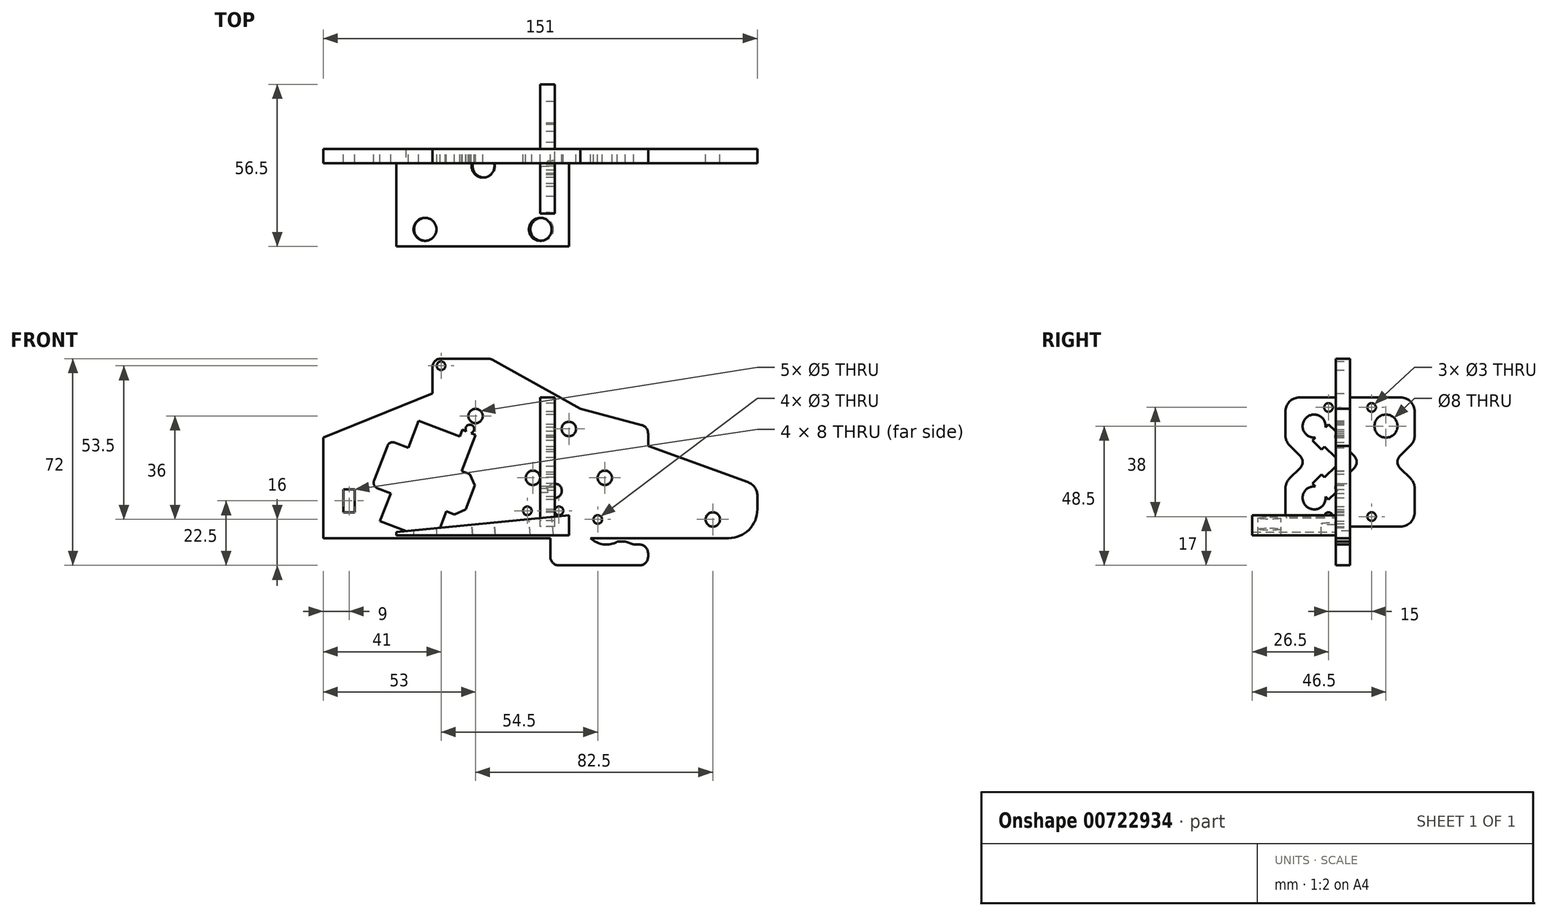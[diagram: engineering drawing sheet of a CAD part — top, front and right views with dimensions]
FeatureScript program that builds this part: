
annotation { "Feature Type Name" : "Feature", "Feature Type Description" : "" }
export const myFeature = defineFeature(function(context is Context, id is Id, definition is map)
    precondition{}
    {
        {
            var Q0;
            Q0=qCreatedBy(makeId("Front.planeOp"),FACE);
            var sketch = newSketch(context, id + "F0", { "sketchPlane" : qUnion([Q0])});
            skLineSegment(sketch, "E0", {"start": v(-50.05, -25.56) * mm, "end": v(9.95, -25.56) * mm});
            skLineSegment(sketch, "E1", {"start": v(9.95, -25.56) * mm, "end": v(9.95, -18.56) * mm});
            skLineSegment(sketch, "E2", {"start": v(-50.05, -25.56) * mm, "end": v(-50.05, -24.36) * mm});
            skLineSegment(sketch, "E3", {"start": v(9.95, -18.56) * mm, "end": v(-50.05, -24.36) * mm});
            skSolve(sketch);
        }
        {
            var Q0;
            Q0=makeQuery(id+"F0.imprint","IMPRINT",FACE,{"disambiguationData":[TD([[makeQuery(id+"F0.imprint","IMPRINT",EDGE,{"derivedFrom":sQuery(id+"F0.wireOp",EDGE,"E0")}),1.0]])]});
            extrude(context, id + "F1", {"entities" : qUnion([Q0]), "depth" : 34 * mm, "offsetDistance" : 25 * mm});
        }
        {
            var Q0;
            Q0=makeQuery(id+"F1.opExtrude","SWEPT_FACE",FACE,{"disambiguationData":[OSD([sQuery(id+"F0.wireOp",EDGE,"E3")])]});
            var sketch = newSketch(context, id + "F2", { "sketchPlane" : qUnion([Q0])});
            skCircle(sketch, "E4", {"center": v(-21.89, -6) * mm, "radius": 4 * mm});
            skCircle(sketch, "E5", {"center": v(-42.17, -28) * mm, "radius": 4 * mm});
            skCircle(sketch, "E6", {"center": v(-1.89, -28) * mm, "radius": 4 * mm});
            skSolve(sketch);
        }
        {
            var Q0;
            Q0 = qSketchRegion(id + "F2", true);
            extrude(context, id + "F3", {"entities" : qUnion([Q0]), "operationType" : NewBodyOperationType.REMOVE, "endBound" : BoundingType.THROUGH_ALL, "oppositeDirection" : true, "depth" : 25 * mm, "offsetDistance" : 25 * mm});
        }
        {
            var Q0;
            Q0=qCreatedBy(makeId("Front.planeOp"),FACE);
            var sketch = newSketch(context, id + "F4", { "sketchPlane" : qUnion([Q0])});
            skCircle(sketch, "E7", {"center": v(-68.5, -1) * mm, "radius": 2.5 * mm});
            skCircle(sketch, "E8", {"center": v(-22.5, 16) * mm, "radius": 2.5 * mm});
            skCircle(sketch, "E9", {"center": v(5, -10) * mm, "radius": 2.5 * mm});
            skCircle(sketch, "E10", {"center": v(20, -20) * mm, "radius": 1.5 * mm});
            skCircle(sketch, "E11", {"center": v(60, -20) * mm, "radius": 2.5 * mm});
            skArc(sketch, "E12", {"start": v(-50.58, 6.78) * mm, "mid": v(-52.11, 6.74) * mm, "end": v(-53.17, 5.63) * mm});
            skArc(sketch, "E13", {"start": v(-57.82, -6.5) * mm, "mid": v(-57.78, -8.04) * mm, "end": v(-56.67, -9.1) * mm});
            skArc(sketch, "E14", {"start": v(75.5, -11.74) * mm, "mid": v(74.6, -8.87) * mm, "end": v(72.21, -7.04) * mm});
            skArc(sketch, "E15", {"start": v(65.5, -26.5) * mm, "mid": v(72.57, -23.57) * mm, "end": v(75.5, -16.5) * mm});
            skArc(sketch, "E16", {"start": v(-18.3, 25.9) * mm, "mid": v(-19.98, 26.35) * mm, "end": v(-21.71, 26.5) * mm});
            skArc(sketch, "E17", {"start": v(-29, 26.5) * mm, "mid": v(-30.91, 26.32) * mm, "end": v(-32.75, 25.77) * mm});
            skLineSegment(sketch, "E18", {"start": v(-75.5, 8.5) * mm, "end": v(-32.75, 25.77) * mm});
            skLineSegment(sketch, "E19", {"start": v(-29, 26.5) * mm, "end": v(-21.71, 26.5) * mm});
            skLineSegment(sketch, "E20", {"start": v(-75.5, 8.5) * mm, "end": v(-75.5, -26.5) * mm});
            skLineSegment(sketch, "E21", {"start": v(-75.5, -26.5) * mm, "end": v(65.5, -26.5) * mm});
            skLineSegment(sketch, "E22", {"start": v(75.5, -11.74) * mm, "end": v(75.5, -16.5) * mm});
            skLineSegment(sketch, "E23", {"start": v(-18.3, 25.9) * mm, "end": v(72.21, -7.04) * mm});
            skLineSegment(sketch, "E24", {"start": v(-55.74, -20.62) * mm, "end": v(-46.4, -24.2) * mm});
            skLineSegment(sketch, "E25", {"start": v(-53.17, 5.63) * mm, "end": v(-57.82, -6.5) * mm});
            skLineSegment(sketch, "E26", {"start": v(-68.5, -9.5) * mm, "end": v(-64.5, -9.5) * mm});
            skLineSegment(sketch, "E27", {"start": v(-68.5, -9.5) * mm, "end": v(-68.5, -17.5) * mm});
            skLineSegment(sketch, "E28", {"start": v(-68.5, -17.5) * mm, "end": v(-64.5, -17.5) * mm});
            skLineSegment(sketch, "E29", {"start": v(-64.5, -9.5) * mm, "end": v(-64.5, -17.5) * mm});
            skLineSegment(sketch, "E30", {"start": v(-56.67, -9.1) * mm, "end": v(-52, -10.88) * mm});
            skLineSegment(sketch, "E31", {"start": v(-50.58, 6.78) * mm, "end": v(-45.91, 4.99) * mm});
            skLineSegment(sketch, "E32", {"start": v(-42.3, 14.4) * mm, "end": v(-28.02, 8.9) * mm});
            skLineSegment(sketch, "E33", {"start": v(-26, -16.51) * mm, "end": v(-22.77, -8.11) * mm});
            skLineSegment(sketch, "E34", {"start": v(-29.87, -18.24) * mm, "end": v(-32.67, -17.16) * mm});
            skLineSegment(sketch, "E35", {"start": v(-27.3, -3.16) * mm, "end": v(-24.5, -4.24) * mm});
            skLineSegment(sketch, "E36", {"start": v(-27.3, -3.16) * mm, "end": v(-23.35, 7.12) * mm});
            skLineSegment(sketch, "E37", {"start": v(-45.91, 4.99) * mm, "end": v(-42.3, 14.4) * mm});
            skLineSegment(sketch, "E38", {"start": v(-24.5, -4.24) * mm, "end": v(-22.77, -8.11) * mm});
            skLineSegment(sketch, "E39", {"start": v(-26, -16.51) * mm, "end": v(-29.87, -18.24) * mm});
            skLineSegment(sketch, "E40", {"start": v(-52, -10.88) * mm, "end": v(-55.74, -20.62) * mm});
            skLineSegment(sketch, "E41", {"start": v(-28.02, 8.9) * mm, "end": v(-27.12, 11.24) * mm});
            skLineSegment(sketch, "E42", {"start": v(-27.12, 11.24) * mm, "end": v(-22.46, 9.45) * mm});
            skLineSegment(sketch, "E43", {"start": v(-23.35, 7.12) * mm, "end": v(-22.46, 9.45) * mm});
            skLineSegment(sketch, "E44", {"start": v(-35.9, -25.56) * mm, "end": v(-40.56, -23.77) * mm});
            skLineSegment(sketch, "E45", {"start": v(-46.4, -24.2) * mm, "end": v(-40.56, -23.77) * mm});
            skLineSegment(sketch, "E46", {"start": v(-35.9, -25.56) * mm, "end": v(-32.67, -17.16) * mm});
            skSolve(sketch);
        }
        {
            var Q0;
            Q0=makeQuery(id+"F4.imprint","IMPRINT",FACE,{"disambiguationData":[TD([[makeQuery(id+"F4.imprint","IMPRINT",EDGE,{"derivedFrom":sQuery(id+"F4.wireOp",EDGE,"E7")}),1.0]])]});
            extrude(context, id + "F5", {"entities" : qUnion([Q0]), "operationType" : NewBodyOperationType.ADD, "depth" : 5 * mm, "offsetDistance" : 25 * mm});
        }
        {
            var Q0;
            Q0=qCreatedBy(makeId("Front.planeOp"),FACE);
            var sketch = newSketch(context, id + "F6", { "sketchPlane" : qUnion([Q0])});
            skCircle(sketch, "E47", {"center": v(-68.5, -1) * mm, "radius": 2.5 * mm});
            skCircle(sketch, "E48", {"center": v(-22.5, 16) * mm, "radius": 2.5 * mm});
            skCircle(sketch, "E49", {"center": v(5, -10) * mm, "radius": 2.5 * mm});
            skCircle(sketch, "E50", {"center": v(20, -20) * mm, "radius": 1.5 * mm});
            skCircle(sketch, "E51", {"center": v(60, -20) * mm, "radius": 2.5 * mm});
            skArc(sketch, "E52", {"start": v(-50.58, 6.78) * mm, "mid": v(-52.11, 6.74) * mm, "end": v(-53.17, 5.63) * mm});
            skArc(sketch, "E53", {"start": v(-57.82, -6.5) * mm, "mid": v(-57.78, -8.04) * mm, "end": v(-56.67, -9.1) * mm});
            skArc(sketch, "E54", {"start": v(75.5, -11.74) * mm, "mid": v(74.6, -8.87) * mm, "end": v(72.21, -7.04) * mm});
            skArc(sketch, "E55", {"start": v(65.5, -26.5) * mm, "mid": v(72.57, -23.57) * mm, "end": v(75.5, -16.5) * mm});
            skArc(sketch, "E56", {"start": v(-18.3, 25.9) * mm, "mid": v(-19.98, 26.35) * mm, "end": v(-21.71, 26.5) * mm});
            skArc(sketch, "E57", {"start": v(-29, 26.5) * mm, "mid": v(-30.91, 26.32) * mm, "end": v(-32.75, 25.77) * mm});
            skLineSegment(sketch, "E58", {"start": v(-75.5, 8.5) * mm, "end": v(-32.75, 25.77) * mm});
            skLineSegment(sketch, "E59", {"start": v(-29, 26.5) * mm, "end": v(-21.71, 26.5) * mm});
            skLineSegment(sketch, "E60", {"start": v(-75.5, 8.5) * mm, "end": v(-75.5, -26.5) * mm});
            skLineSegment(sketch, "E61", {"start": v(-75.5, -26.5) * mm, "end": v(65.5, -26.5) * mm});
            skLineSegment(sketch, "E62", {"start": v(75.5, -11.74) * mm, "end": v(75.5, -16.5) * mm});
            skLineSegment(sketch, "E63", {"start": v(-18.3, 25.9) * mm, "end": v(72.21, -7.04) * mm});
            skLineSegment(sketch, "E64", {"start": v(-55.74, -20.62) * mm, "end": v(-46.4, -24.2) * mm});
            skLineSegment(sketch, "E65", {"start": v(-53.17, 5.63) * mm, "end": v(-57.82, -6.5) * mm});
            skLineSegment(sketch, "E66", {"start": v(-68.5, -9.5) * mm, "end": v(-64.5, -9.5) * mm});
            skLineSegment(sketch, "E67", {"start": v(-68.5, -9.5) * mm, "end": v(-68.5, -17.5) * mm});
            skLineSegment(sketch, "E68", {"start": v(-68.5, -17.5) * mm, "end": v(-64.5, -17.5) * mm});
            skLineSegment(sketch, "E69", {"start": v(-64.5, -9.5) * mm, "end": v(-64.5, -17.5) * mm});
            skLineSegment(sketch, "E70", {"start": v(-56.67, -9.1) * mm, "end": v(-52, -10.88) * mm});
            skLineSegment(sketch, "E71", {"start": v(-50.58, 6.78) * mm, "end": v(-45.91, 4.99) * mm});
            skLineSegment(sketch, "E72", {"start": v(-42.3, 14.4) * mm, "end": v(-28.02, 8.9) * mm});
            skLineSegment(sketch, "E73", {"start": v(-26, -16.51) * mm, "end": v(-22.77, -8.11) * mm});
            skLineSegment(sketch, "E74", {"start": v(-29.87, -18.24) * mm, "end": v(-32.67, -17.16) * mm});
            skLineSegment(sketch, "E75", {"start": v(-27.3, -3.16) * mm, "end": v(-24.5, -4.24) * mm});
            skLineSegment(sketch, "E76", {"start": v(-27.3, -3.16) * mm, "end": v(-23.35, 7.12) * mm});
            skLineSegment(sketch, "E77", {"start": v(-45.91, 4.99) * mm, "end": v(-42.3, 14.4) * mm});
            skLineSegment(sketch, "E78", {"start": v(-24.5, -4.24) * mm, "end": v(-22.77, -8.11) * mm});
            skLineSegment(sketch, "E79", {"start": v(-26, -16.51) * mm, "end": v(-29.87, -18.24) * mm});
            skLineSegment(sketch, "E80", {"start": v(-52, -10.88) * mm, "end": v(-55.74, -20.62) * mm});
            skLineSegment(sketch, "E81", {"start": v(-28.02, 8.9) * mm, "end": v(-27.12, 11.24) * mm});
            skLineSegment(sketch, "E82", {"start": v(-27.12, 11.24) * mm, "end": v(-22.46, 9.45) * mm});
            skLineSegment(sketch, "E83", {"start": v(-23.35, 7.12) * mm, "end": v(-22.46, 9.45) * mm});
            skLineSegment(sketch, "E84", {"start": v(-35.9, -25.56) * mm, "end": v(-40.56, -23.77) * mm});
            skLineSegment(sketch, "E85", {"start": v(-46.4, -24.2) * mm, "end": v(-40.56, -23.77) * mm});
            skLineSegment(sketch, "E86", {"start": v(-35.9, -25.56) * mm, "end": v(-32.67, -17.16) * mm});
            skCircle(sketch, "E87", {"center": v(-2.56, -5.5) * mm, "radius": 2.5 * mm});
            skCircle(sketch, "E88", {"center": v(22.44, -5.5) * mm, "radius": 2.5 * mm});
            skCircle(sketch, "E89", {"center": v(-4.5, -17) * mm, "radius": 1.5 * mm});
            skCircle(sketch, "E90", {"center": v(6.5, -17) * mm, "radius": 1.5 * mm});
            skCircle(sketch, "E91", {"center": v(9.94, 11.5) * mm, "radius": 2.5 * mm});
            skCircle(sketch, "E92", {"center": v(-34.5, 33.5) * mm, "radius": 1.5 * mm});
            skCircle(sketch, "E93", {"center": v(-24.5, 11.5) * mm, "radius": 1.5 * mm});
            skArc(sketch, "E94", {"start": v(26.8, -14.25) * mm, "mid": v(15.25, -21) * mm, "end": v(26.8, -27.75) * mm});
            skArc(sketch, "E95", {"start": v(-17.5, 3.5) * mm, "mid": v(-18.96, 7.04) * mm, "end": v(-22.5, 8.5) * mm});
            skArc(sketch, "E96", {"start": v(3.5, -27) * mm, "mid": v(2.04, -23.46) * mm, "end": v(-1.5, -22) * mm});
            skArc(sketch, "E97", {"start": v(34.5, -36) * mm, "mid": v(36.62, -35.12) * mm, "end": v(37.5, -33) * mm});
            skArc(sketch, "E98", {"start": v(-9.5, -19) * mm, "mid": v(-8.62, -21.12) * mm, "end": v(-6.5, -22) * mm});
            skArc(sketch, "E99", {"start": v(-9.5, -16.5) * mm, "mid": v(-10.38, -14.38) * mm, "end": v(-12.5, -13.5) * mm});
            skArc(sketch, "E100", {"start": v(-17.5, -10.5) * mm, "mid": v(-16.62, -12.62) * mm, "end": v(-14.5, -13.5) * mm});
            skArc(sketch, "E101", {"start": v(-37.5, 11.5) * mm, "mid": v(-36.62, 9.38) * mm, "end": v(-34.5, 8.5) * mm});
            skArc(sketch, "E102", {"start": v(3.5, -33) * mm, "mid": v(4.38, -35.12) * mm, "end": v(6.5, -36) * mm});
            skArc(sketch, "E103", {"start": v(34.5, -13.25) * mm, "mid": v(36.62, -12.37) * mm, "end": v(37.5, -10.25) * mm});
            skArc(sketch, "E104", {"start": v(37.5, -31.75) * mm, "mid": v(36.62, -29.63) * mm, "end": v(34.5, -28.75) * mm});
            skArc(sketch, "E105", {"start": v(37.5, 9.95) * mm, "mid": v(36.88, 11.77) * mm, "end": v(35.28, 12.85) * mm});
            skArc(sketch, "E106", {"start": v(-34.5, 36) * mm, "mid": v(-36.62, 35.12) * mm, "end": v(-37.5, 33) * mm});
            skArc(sketch, "E107", {"start": v(-16.82, 35.62) * mm, "mid": v(-17.52, 35.9) * mm, "end": v(-18.28, 36) * mm});
            skLineSegment(sketch, "E108", {"start": v(-34.5, 8.5) * mm, "end": v(-22.5, 8.5) * mm});
            skLineSegment(sketch, "E109", {"start": v(-34.5, 36) * mm, "end": v(-18.28, 36) * mm});
            skLineSegment(sketch, "E110", {"start": v(-37.5, 33) * mm, "end": v(-37.5, 11.5) * mm});
            skLineSegment(sketch, "E111", {"start": v(6.5, -36) * mm, "end": v(34.5, -36) * mm});
            skLineSegment(sketch, "E112", {"start": v(37.5, 9.95) * mm, "end": v(37.5, -10.25) * mm});
            skLineSegment(sketch, "E113", {"start": v(-16.82, 35.62) * mm, "end": v(13.97, 18.55) * mm});
            skLineSegment(sketch, "E114", {"start": v(-17.5, 3.5) * mm, "end": v(-17.5, -10.5) * mm});
            skLineSegment(sketch, "E115", {"start": v(-14.5, -13.5) * mm, "end": v(-12.5, -13.5) * mm});
            skLineSegment(sketch, "E116", {"start": v(-9.5, -16.5) * mm, "end": v(-9.5, -19) * mm});
            skLineSegment(sketch, "E117", {"start": v(-6.5, -22) * mm, "end": v(-1.5, -22) * mm});
            skLineSegment(sketch, "E118", {"start": v(3.5, -27) * mm, "end": v(3.5, -33) * mm});
            skLineSegment(sketch, "E119", {"start": v(26.8, -14.25) * mm, "end": v(29.5, -14.25) * mm});
            skLineSegment(sketch, "E120", {"start": v(32.5, -13.25) * mm, "end": v(34.5, -13.25) * mm});
            skLineSegment(sketch, "E121", {"start": v(29.5, -14.25) * mm, "end": v(32.5, -13.25) * mm});
            skLineSegment(sketch, "E122", {"start": v(32.5, -28.75) * mm, "end": v(34.5, -28.75) * mm});
            skLineSegment(sketch, "E123", {"start": v(29.5, -27.75) * mm, "end": v(32.5, -28.75) * mm});
            skLineSegment(sketch, "E124", {"start": v(26.8, -27.75) * mm, "end": v(29.5, -27.75) * mm});
            skLineSegment(sketch, "E125", {"start": v(37.5, -31.75) * mm, "end": v(37.5, -33) * mm});
            skLineSegment(sketch, "E126", {"start": v(13.97, 18.55) * mm, "end": v(35.28, 12.85) * mm});
            skSolve(sketch);
        }
        {
            var Q0;
            Q0 = qSketchRegion(id + "F6", true);
            extrude(context, id + "F7", {"entities" : qUnion([Q0]), "operationType" : NewBodyOperationType.ADD, "depth" : 5 * mm, "offsetDistance" : 25 * mm});
        }
        {
            var Q0;
            Q0=qCreatedBy(makeId("Right.planeOp"),FACE);
            var sketch = newSketch(context, id + "F8", { "sketchPlane" : qUnion([Q0])});
            skArc(sketch, "E127", {"start": v(-12.06, -8.52) * mm, "mid": v(-15.33, -15.33) * mm, "end": v(-8.52, -12.06) * mm});
            skArc(sketch, "E128", {"start": v(22.5, 17.5) * mm, "mid": v(21.04, 21.04) * mm, "end": v(17.5, 22.5) * mm});
            skArc(sketch, "E129", {"start": v(-8.52, 12.06) * mm, "mid": v(-15.33, 15.33) * mm, "end": v(-12.06, 8.52) * mm});
            skCircle(sketch, "E130", {"center": v(-7.5, -19) * mm, "radius": 1.5 * mm});
            skArc(sketch, "E131", {"start": v(1.41, -2.12) * mm, "mid": v(2.3, 0) * mm, "end": v(1.41, 2.12) * mm});
            skCircle(sketch, "E132", {"center": v(7.5, -19) * mm, "radius": 1.5 * mm});
            skCircle(sketch, "E133", {"center": v(7.5, 19) * mm, "radius": 1.5 * mm});
            skCircle(sketch, "E134", {"center": v(-7.5, 19) * mm, "radius": 1.5 * mm});
            skCircle(sketch, "E135", {"center": v(12.5, 12.5) * mm, "radius": 4 * mm});
            skArc(sketch, "E136", {"start": v(17.5, -22.5) * mm, "mid": v(21.04, -21.04) * mm, "end": v(22.5, -17.5) * mm});
            skArc(sketch, "E137", {"start": v(-22.5, -17.5) * mm, "mid": v(-21.04, -21.04) * mm, "end": v(-17.5, -22.5) * mm});
            skArc(sketch, "E138", {"start": v(-17.5, 22.5) * mm, "mid": v(-21.04, 21.04) * mm, "end": v(-22.5, 17.5) * mm});
            skArc(sketch, "E139", {"start": v(17.38, 2.12) * mm, "mid": v(16.5, 0) * mm, "end": v(17.38, -2.12) * mm});
            skArc(sketch, "E140", {"start": v(-17.38, -2.12) * mm, "mid": v(-16.5, 0) * mm, "end": v(-17.38, 2.12) * mm});
            skArc(sketch, "E141", {"start": v(22.5, -9.31) * mm, "mid": v(22.12, -7.4) * mm, "end": v(21.04, -5.78) * mm});
            skArc(sketch, "E142", {"start": v(21.04, 5.78) * mm, "mid": v(22.12, 7.4) * mm, "end": v(22.5, 9.31) * mm});
            skArc(sketch, "E143", {"start": v(-21.04, -5.78) * mm, "mid": v(-22.12, -7.4) * mm, "end": v(-22.5, -9.31) * mm});
            skArc(sketch, "E144", {"start": v(-22.5, 9.31) * mm, "mid": v(-22.12, 7.4) * mm, "end": v(-21.04, 5.78) * mm});
            skLineSegment(sketch, "E145", {"start": v(-17.5, 22.5) * mm, "end": v(-2.47, 22.5) * mm});
            skLineSegment(sketch, "E146", {"start": v(-22.5, 17.5) * mm, "end": v(-22.5, 9.31) * mm});
            skLineSegment(sketch, "E147", {"start": v(-17.5, -22.5) * mm, "end": v(17.5, -22.5) * mm});
            skLineSegment(sketch, "E148", {"start": v(22.5, -9.31) * mm, "end": v(22.5, -17.5) * mm});
            skLineSegment(sketch, "E149", {"start": v(-8.88, 5.34) * mm, "end": v(-3.54, 0) * mm});
            skLineSegment(sketch, "E150", {"start": v(-5.34, -8.88) * mm, "end": v(1.41, -2.12) * mm});
            skLineSegment(sketch, "E151", {"start": v(-8.52, -12.06) * mm, "end": v(-7.46, -13.12) * mm});
            skLineSegment(sketch, "E152", {"start": v(-7.46, -13.12) * mm, "end": v(-4.28, -9.94) * mm});
            skLineSegment(sketch, "E153", {"start": v(-13.12, -7.46) * mm, "end": v(-9.94, -4.28) * mm});
            skLineSegment(sketch, "E154", {"start": v(-12.06, -8.52) * mm, "end": v(-13.12, -7.46) * mm});
            skLineSegment(sketch, "E155", {"start": v(-9.94, -4.28) * mm, "end": v(-8.88, -5.34) * mm});
            skLineSegment(sketch, "E156", {"start": v(-5.34, -8.88) * mm, "end": v(-4.28, -9.94) * mm});
            skLineSegment(sketch, "E157", {"start": v(-8.88, -5.34) * mm, "end": v(-3.54, 0) * mm});
            skLineSegment(sketch, "E158", {"start": v(-5.34, 8.88) * mm, "end": v(-4.28, 9.94) * mm});
            skLineSegment(sketch, "E159", {"start": v(-9.94, 4.28) * mm, "end": v(-8.88, 5.34) * mm});
            skLineSegment(sketch, "E160", {"start": v(-12.06, 8.52) * mm, "end": v(-13.12, 7.46) * mm});
            skLineSegment(sketch, "E161", {"start": v(-7.46, 13.12) * mm, "end": v(-4.28, 9.94) * mm});
            skLineSegment(sketch, "E162", {"start": v(-8.52, 12.06) * mm, "end": v(-7.46, 13.12) * mm});
            skLineSegment(sketch, "E163", {"start": v(-5.34, 8.88) * mm, "end": v(1.41, 2.12) * mm});
            skLineSegment(sketch, "E164", {"start": v(-13.12, 7.46) * mm, "end": v(-9.94, 4.28) * mm});
            skLineSegment(sketch, "E165", {"start": v(-2.47, 22.5) * mm, "end": v(17.5, 22.5) * mm});
            skLineSegment(sketch, "E166", {"start": v(-17.38, -2.12) * mm, "end": v(-21.04, -5.78) * mm});
            skLineSegment(sketch, "E167", {"start": v(17.38, 2.12) * mm, "end": v(21.04, 5.78) * mm});
            skLineSegment(sketch, "E168", {"start": v(17.38, -2.12) * mm, "end": v(21.04, -5.78) * mm});
            skLineSegment(sketch, "E169", {"start": v(22.5, 9.31) * mm, "end": v(22.5, 17.5) * mm});
            skLineSegment(sketch, "E170", {"start": v(-17.38, 2.12) * mm, "end": v(-21.04, 5.78) * mm});
            skLineSegment(sketch, "E171", {"start": v(-22.5, -9.31) * mm, "end": v(-22.5, -17.5) * mm});
            skSolve(sketch);
        }
        {
            var Q0;
            Q0 = qSketchRegion(id + "F8", true);
            extrude(context, id + "F9", {"entities" : qUnion([Q0]), "operationType" : NewBodyOperationType.ADD, "depth" : 5 * mm, "offsetDistance" : 25 * mm});
        }
    });
